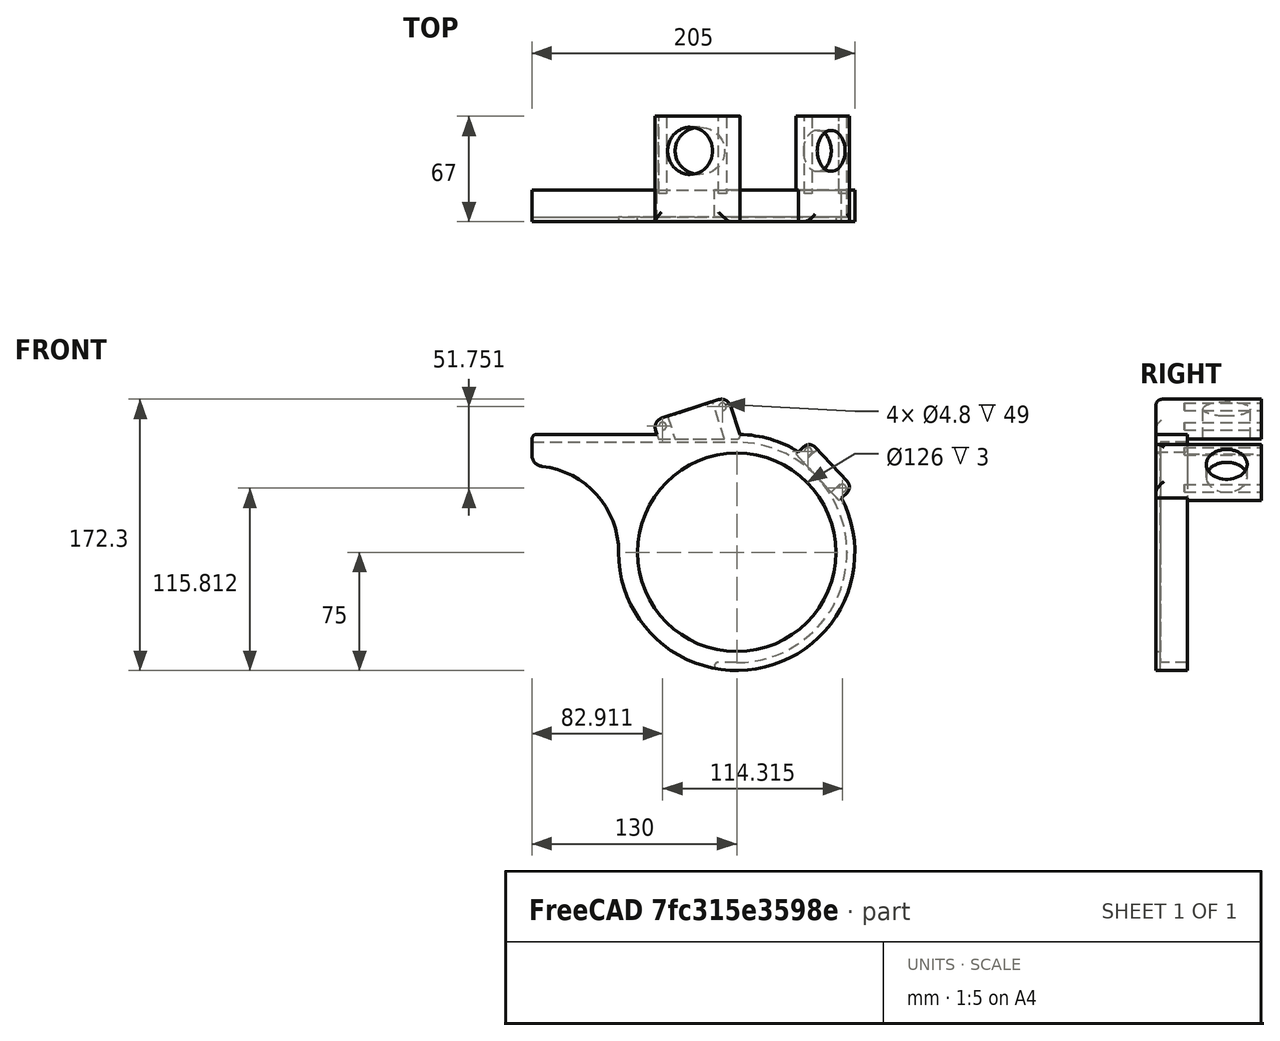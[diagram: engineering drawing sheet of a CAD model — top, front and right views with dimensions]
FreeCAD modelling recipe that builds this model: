
FCSTD DOCUMENT  (FreeCAD 0.19R)
Label: WhiteBike2
License: All rights reserved
LicenseURL: http://en.wikipedia.org/wiki/All_rights_reserved
objects: Sketcher::SketchObject×6, PartDesign::Fillet×6, PartDesign::Pocket×4, PartDesign::Pad×2, PartDesign::Body×1
note: 31 computed .brp shape members not serialized (recipe doc carries the construction recipe); baked Part::Feature solids carry a one-line shape summary decoded from their .brp

FEATURE [Sketcher::SketchObject] Sketch
  FullyConstrained = true
  MapMode = 5
  Placement = pos=(0,0,0) rot=(1,0,0;1.5708rad)
  Support = -> [XZ_Plane]
  sketch-geometry (5):
    g0: Circle CenterX=0 CenterY=0 CenterZ=0 NormalX=0 NormalY=0 NormalZ=1 AngleXU=0 Radius=63
    g1: ArcOfCircle CenterX=0 CenterY=0 CenterZ=0 NormalX=0 NormalY=0 NormalZ=1 AngleXU=0 Radius=75 StartAngle=3.14159 EndAngle=7.85398
    g2: LineSegment StartX=2.3e-14 StartY=75 StartZ=0 EndX=-130 EndY=75 EndZ=0
    g3: LineSegment StartX=-130 StartY=75 StartZ=0 EndX=-130 EndY=55 EndZ=0
    g4: ArcOfCircle CenterX=-130 CenterY=6.7e-15 CenterZ=0 NormalX=0 NormalY=0 NormalZ=1 AngleXU=0 Radius=55 StartAngle=0 EndAngle=1.5708
  constraints (14):
    c: Coincident(g0,g-1)
    c: Coincident(g1,g0)
    c: PointOnObject(g1,g-2)
    c: Coincident(g2,g1)
    c: Horizontal(g2)
    c: Coincident(g2,g3)
    c: Vertical(g3)
    c: Coincident(g4,g3)
    c: Tangent(g1,g4) = 1.5708
    c: Distance(g2) = 130
    c: Perpendicular(g4,g3)
    c: Radius(g0) = 63
    c: Radius(g1) = 75
    c: PointOnObject(g1,g-1)
FEATURE [PartDesign::Pad] Pad
  Direction = (1,1,1)
  Length = 20
  Length2 = 100
  Placement = pos=(0,0,0) rot=(1,0,0;1.5708rad)
  Profile = -> Sketch
  Type = 0
FEATURE [Sketcher::SketchObject] Sketch001
  FullyConstrained = true
  MapMode = 5
  Placement = pos=(0,0,0) rot=(-1,0,0;1.5708rad)
  Support = -> [Pad]
  sketch-geometry (4):
    g0: ArcOfCircle CenterX=0 CenterY=0 CenterZ=0 NormalX=0 NormalY=0 NormalZ=1 AngleXU=0 Radius=70 StartAngle=4.71239 EndAngle=7.85398
    g1: LineSegment StartX=2.14e-14 StartY=70 StartZ=0 EndX=-174.45 EndY=70 EndZ=0
    g2: LineSegment StartX=-174.45 StartY=70 StartZ=0 EndX=-174.45 EndY=-70 EndZ=0
    g3: LineSegment StartX=-174.45 StartY=-70 StartZ=0 EndX=0 EndY=-70 EndZ=0
  constraints (11):
    c: Coincident(g0,g-1)
    c: PointOnObject(g0,g-2)
    c: PointOnObject(g0,g-2)
    c: Radius(g0) = 70
    c: Tangent(g0,g1) = -1.5708
    c: Coincident(g1,g2)
    c: Vertical(g2)
    c: Coincident(g2,g3)
    c: Coincident(g3,g0)
    c: Horizontal(g3)
    c: Distance(g1) = 174.45
FEATURE [PartDesign::Pocket] Pocket
  BaseFeature = -> Pad
  Length = 17
  Length2 = 100
  Placement = pos=(0,0,0) rot=(1,0,0;1.5708rad)
  Profile = -> Sketch001
  Type = 0
FEATURE [Sketcher::SketchObject] Sketch002
  ExternalGeometry = -> [Pocket]
  FullyConstrained = true
  MapMode = 5
  Placement = pos=(0,0,0) rot=(-1,0,0;1.5708rad)
  Support = -> [Pocket]
  sketch-geometry (10):
    g0: LineSegment StartX=0 StartY=0 StartZ=0 EndX=219.406 EndY=-204.6 EndZ=0
    g1: LineSegment StartX=-61.8034 StartY=-190.211 StartZ=0 EndX=7.1e-15 EndY=0 EndZ=0
    g2: LineSegment StartX=-5.83615 StartY=-98.8635 StartZ=0 EndX=-53.389 EndY=-83.4127 EndZ=0
    g3: LineSegment StartX=-53.389 StartY=-83.4127 StartZ=0 EndX=-49.6808 EndY=-72 EndZ=0
    g4: LineSegment StartX=-49.6808 StartY=-72 StartZ=0 EndX=2.89234 EndY=-72 EndZ=0
    g5: LineSegment StartX=2.89234 StartY=-72 StartZ=0 EndX=-5.83615 EndY=-98.8635 EndZ=0
    g6: LineSegment StartX=73.611 StartY=-41.2968 StartZ=0 EndX=46.331 EndY=-70.5509 EndZ=0
    g7: LineSegment StartX=46.331 StartY=-70.5509 StartZ=0 EndX=37.5548 EndY=-62.367 EndZ=0
    g8: LineSegment StartX=37.5548 StartY=-62.367 StartZ=0 EndX=64.8347 EndY=-33.1128 EndZ=0
    g9: LineSegment StartX=64.8347 StartY=-33.1128 StartZ=0 EndX=73.611 EndY=-41.2968 EndZ=0
  constraints (28):
    c: Coincident(g0,g-1)
    c: Coincident(g1,g-1)
    c: Angle(g1) = 1.25664
    c: Distance(g1) = 200
    c: Distance(g0) = 300
    c: Coincident(g2,g3)
    c: Coincident(g3,g4)
    c: Coincident(g4,g5)
    c: Coincident(g5,g2)
    c: Coincident(g6,g7)
    c: Coincident(g7,g8)
    c: Coincident(g8,g9)
    c: Coincident(g9,g6)
    c: Equal(g8,g6)
    c: Perpendicular(g0,g8)
    c: Perpendicular(g9,g6)
    c: Symmetric(g6,g6,g0)
    c: Distance(g7) = 12
    c: Distance(g6) = 40
    c: Perpendicular(g3,g2)
    c: Perpendicular(g5,g2)
    c: Parallel(g-3,g4)
    c: Symmetric(g2,g2,g1)
    c: Distance(g3) = 12
    c: Distance(g4,g-3) = 3
    c: Tangent(g8,g-4)
    c: Distance(g2) = 50
    c: Angle(g1,g0) = 1.13446
FEATURE [PartDesign::Pad] Pad001
  BaseFeature = -> Pocket
  Direction = (1,1,1)
  Length = 47
  Length2 = 20
  Placement = pos=(0,0,0) rot=(1,0,0;1.5708rad)
  Profile = -> Sketch002
  Type = 4
FEATURE [Sketcher::SketchObject] Sketch006
  FullyConstrained = true
  MapMode = 5
  Placement = pos=(-29.6126,1.417e-13,91.1381) rot=(-0.156434,0,0.987688;3.14159rad)
  Support = -> [Pad001]
  sketch-geometry (1):
    g0: Circle CenterX=0 CenterY=-25 CenterZ=0 NormalX=0 NormalY=0 NormalZ=1 AngleXU=0 Radius=15
  constraints (3):
    c: Radius(g0) = 15
    c: PointOnObject(g0,g-2)
    c: DistanceY(g0) = -25
FEATURE [PartDesign::Pocket] Pocket001
  BaseFeature = -> Pad001
  Length = 5
  Length2 = 100
  Placement = pos=(0,0,0) rot=(1,0,0;1.5708rad)
  Profile = -> Sketch006
  Type = 1
FEATURE [Sketcher::SketchObject] Sketch007
  FullyConstrained = true
  MapMode = 5
  Placement = pos=(59.971,1.118e-13,55.9239) rot=(0.398749,0,0.91706;3.14159rad)
  Support = -> [Pocket001]
  sketch-geometry (1):
    g0: Circle CenterX=0 CenterY=-25 CenterZ=0 NormalX=0 NormalY=0 NormalZ=1 AngleXU=0 Radius=13
  constraints (3):
    c: Radius(g0) = 13
    c: PointOnObject(g0,g-2)
    c: DistanceY(g0) = -25
FEATURE [PartDesign::Pocket] Pocket002
  BaseFeature = -> Pocket001
  Length = 5
  Length2 = 100
  Placement = pos=(0,0,0) rot=(1,0,0;1.5708rad)
  Profile = -> Sketch007
  Type = 1
FEATURE [Sketcher::SketchObject] Sketch008
  ExternalGeometry = -> [Pocket002]
  FullyConstrained = true
  MapMode = 5
  Placement = pos=(0,47,-1.148e-13) rot=(-1,0,0;1.5708rad)
  Support = -> [Pocket002]
  sketch-geometry (4):
    g0: Circle CenterX=67.2262 CenterY=-40.8122 CenterZ=0 NormalX=0 NormalY=0 NormalZ=1 AngleXU=0 Radius=2.4
    g1: Circle CenterX=45.4023 CenterY=-64.2155 CenterZ=0 NormalX=0 NormalY=0 NormalZ=1 AngleXU=0 Radius=2.4
    g2: Circle CenterX=-9.04635 CenterY=-92.5632 CenterZ=0 NormalX=0 NormalY=0 NormalZ=1 AngleXU=0 Radius=2.4
    g3: Circle CenterX=-47.0886 CenterY=-80.2025 CenterZ=0 NormalX=0 NormalY=0 NormalZ=1 AngleXU=0 Radius=2.4
  constraints (12):
    c: Radius(g3) = 2.4
    c: Equal(g3,g2)
    c: Equal(g3,g1)
    c: Equal(g3,g0)
    c: Distance(g1,g-5) = 5
    c: Distance(g0,g-5) = 5
    c: Distance(g0,g-3) = 4
    c: Distance(g1,g-4) = 4
    c: Distance(g2,g-7) = 5
    c: Distance(g3,g-6) = 5
    c: Distance(g2,g-6) = 5
    c: Distance(g3,g-8) = 5
FEATURE [PartDesign::Pocket] Pocket003
  BaseFeature = -> Pocket002
  Length = 49
  Length2 = 100
  Placement = pos=(0,0,0) rot=(1,0,0;1.5708rad)
  Profile = -> Sketch008
  Type = 0
FEATURE [PartDesign::Fillet] Fillet
  Base = -> Pocket003 [Edge77,Edge78,Edge75]
  BaseFeature = -> Pocket003
  Placement = pos=(0,0,0) rot=(1,0,0;1.5708rad)
  Radius = 6
  SupportTransform = false
FEATURE [PartDesign::Fillet] Fillet001
  Base = -> Fillet [Edge65,Edge85,Edge90]
  BaseFeature = -> Fillet
  Placement = pos=(0,0,0) rot=(1,0,0;1.5708rad)
  Radius = 5
  SupportTransform = false
FEATURE [PartDesign::Fillet] Fillet002
  Base = -> Fillet001 [Edge66]
  BaseFeature = -> Fillet001
  Placement = pos=(0,0,0) rot=(1,0,0;1.5708rad)
  Radius = 3
  SupportTransform = false
FEATURE [PartDesign::Fillet] Fillet003
  Base = -> Fillet002 [Edge16]
  BaseFeature = -> Fillet002
  Placement = pos=(0,0,0) rot=(1,0,0;1.5708rad)
  Radius = 7
  SupportTransform = false
FEATURE [PartDesign::Fillet] Fillet004
  Base = -> Fillet003 [Edge43]
  BaseFeature = -> Fillet003
  Placement = pos=(0,0,0) rot=(1,0,0;1.5708rad)
  Radius = 2
  SupportTransform = false
FEATURE [PartDesign::Fillet] Fillet005
  Base = -> Fillet004 [Edge83]
  BaseFeature = -> Fillet004
  Placement = pos=(0,0,0) rot=(1,0,0;1.5708rad)
  Radius = 2
  SupportTransform = false
FEATURE [PartDesign::Body] Body
  Group = -> [Sketch,Pad,Sketch001,Pocket,Sketch002,Pad001,Sketch006,Pocket001,Sketch007,Pocket002,Sketch008,Pocket003,Fillet,Fillet001,Fillet002,Fillet003,Fillet004,Fillet005]
  Origin = -> Origin
  Tip = -> Fillet005
